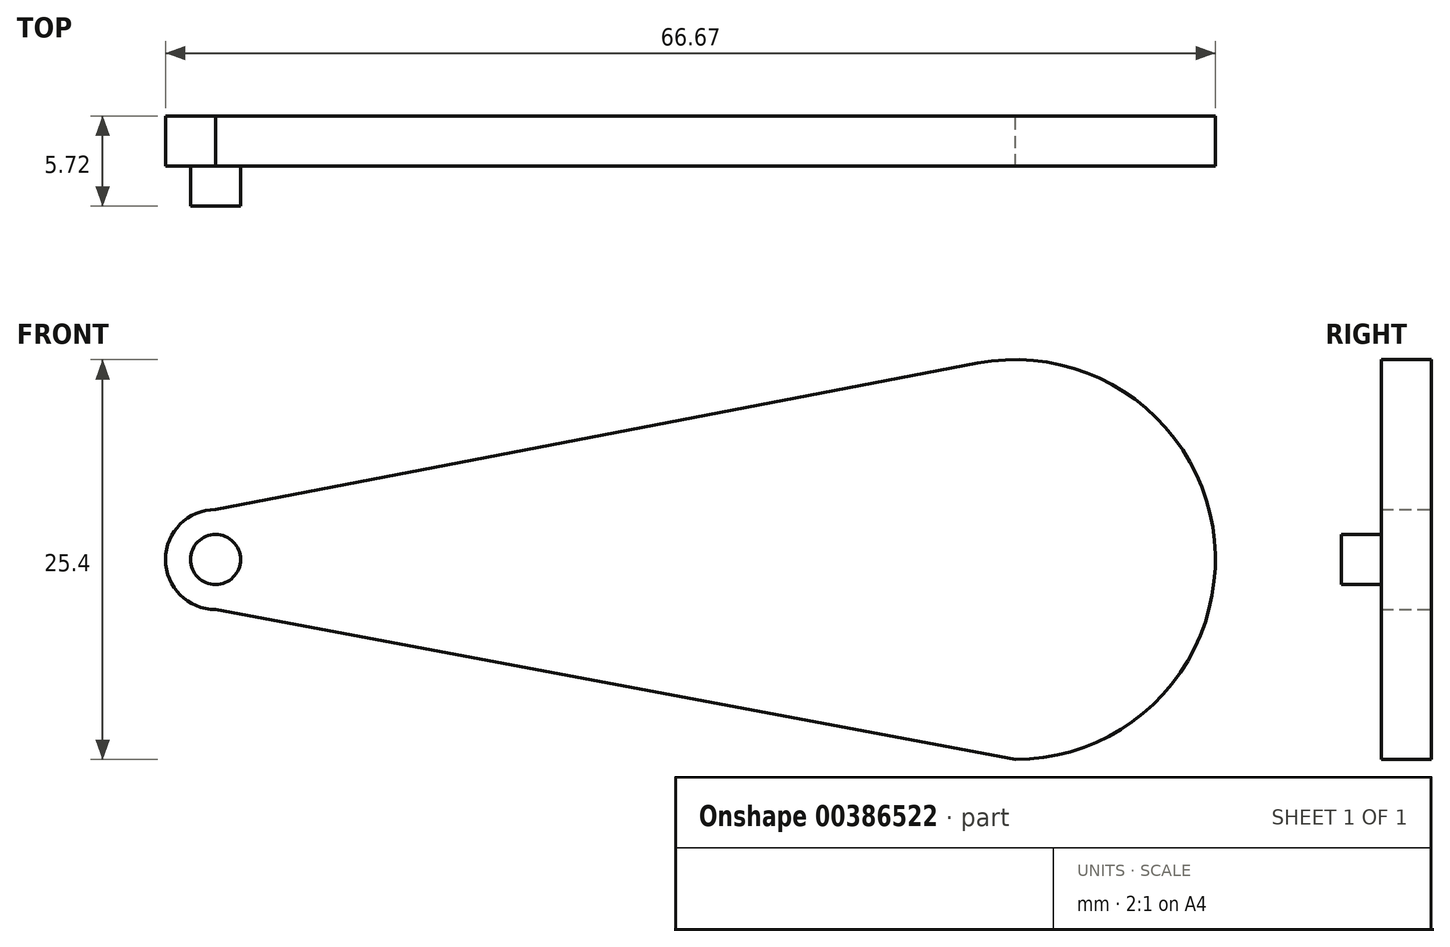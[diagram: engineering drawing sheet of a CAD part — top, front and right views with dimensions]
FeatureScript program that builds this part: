
annotation { "Feature Type Name" : "Feature", "Feature Type Description" : "" }
export const myFeature = defineFeature(function(context is Context, id is Id, definition is map)
    precondition{}
    {
        {
            var Q0;
            Q0=qCreatedBy(makeId("Front.planeOp"),FACE);
            var sketch = newSketch(context, id + "F0", { "sketchPlane" : qUnion([Q0])});
            skArc(sketch, "E0", {"start": v(0, 3.18) * mm, "mid": v(-3.18, 0) * mm, "end": v(0, -3.18) * mm});
            skArc(sketch, "E1", {"start": v(50.8, -12.7) * mm, "mid": v(63.44, 1.2) * mm, "end": v(48.4, 12.47) * mm});
            skLineSegment(sketch, "E2", {"start": v(0, 3.17) * mm, "end": v(48.4, 12.47) * mm});
            skLineSegment(sketch, "E3", {"start": v(0, -3.17) * mm, "end": v(50.8, -12.7) * mm});
            skPoint(sketch, "E4.orphan", {"position": v(50.8, 12.93) * mm});
            skSolve(sketch);
        }
        {
            var Q0;
            Q0 = qSketchRegion(id + "F0", true);
            extrude(context, id + "F1", {"entities" : qUnion([Q0]), "depth" : 3.17 * mm});
        }
        {
            var Q0;
            Q0=makeQuery(id+"F1.opExtrude","CAP_FACE",FACE,{"disambiguationData":[OSD([sQuery(id+"F0.wireOp",EDGE,"E0"),sQuery(id+"F0.wireOp",EDGE,"E1"),sQuery(id+"F0.wireOp",EDGE,"E2"),sQuery(id+"F0.wireOp",EDGE,"E3")])],"isStart":false});
            var sketch = newSketch(context, id + "F2", { "sketchPlane" : qUnion([Q0])});
            skCircle(sketch, "E5", {"center": v(0, 0) * mm, "radius": 1.59 * mm});
            skSolve(sketch);
        }
        {
            var Q0;
            Q0 = qSketchRegion(id + "F2", true);
            extrude(context, id + "F3", {"entities" : qUnion([Q0]), "operationType" : NewBodyOperationType.ADD, "depth" : 2.54 * mm});
        }
    });
